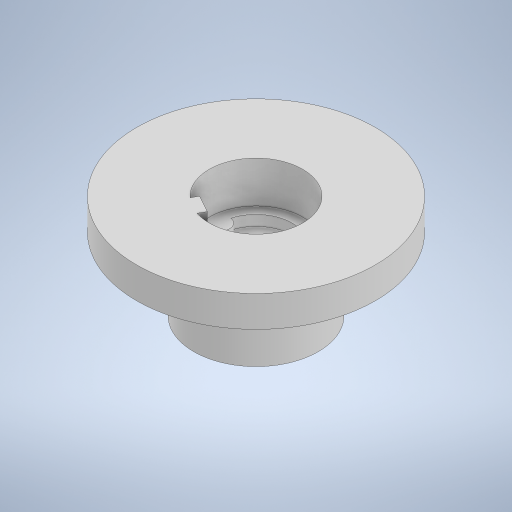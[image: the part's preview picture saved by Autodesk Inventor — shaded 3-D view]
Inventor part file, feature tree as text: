
AUTODESK INVENTOR PART (.ipt)
format: ipt  version: 2023 (Build 270158000, 158)  size: 270,336 bytes
history: native  units: mm
features: extrude x5, sketch x5, other x1
ambient origin geometry x8: Origin, YZ Plane, XZ Plane, XY Plane, X Axis, Y Axis, Z Axis, Center Point
bodies: Body1 (feature_tree)
feature tree (11):
  other  "Твердое тело1"
  extrude  "Выдавливание1"  Depth=7.0mm
  extrude  "Выдавливание2"  Depth=1.9mm
  extrude  "Выдавливание3"  Depth=30.0mm TaperAngle=360.0deg
  extrude  "Выдавливание4"  Depth=9.0mm
  extrude  "Выдавливание5"  Depth=3.0mm
  sketch  "Эскиз1"
  sketch  "Эскиз2"
  sketch  "Эскиз3"
  sketch  "Эскиз4"
  sketch  "Эскиз5"
